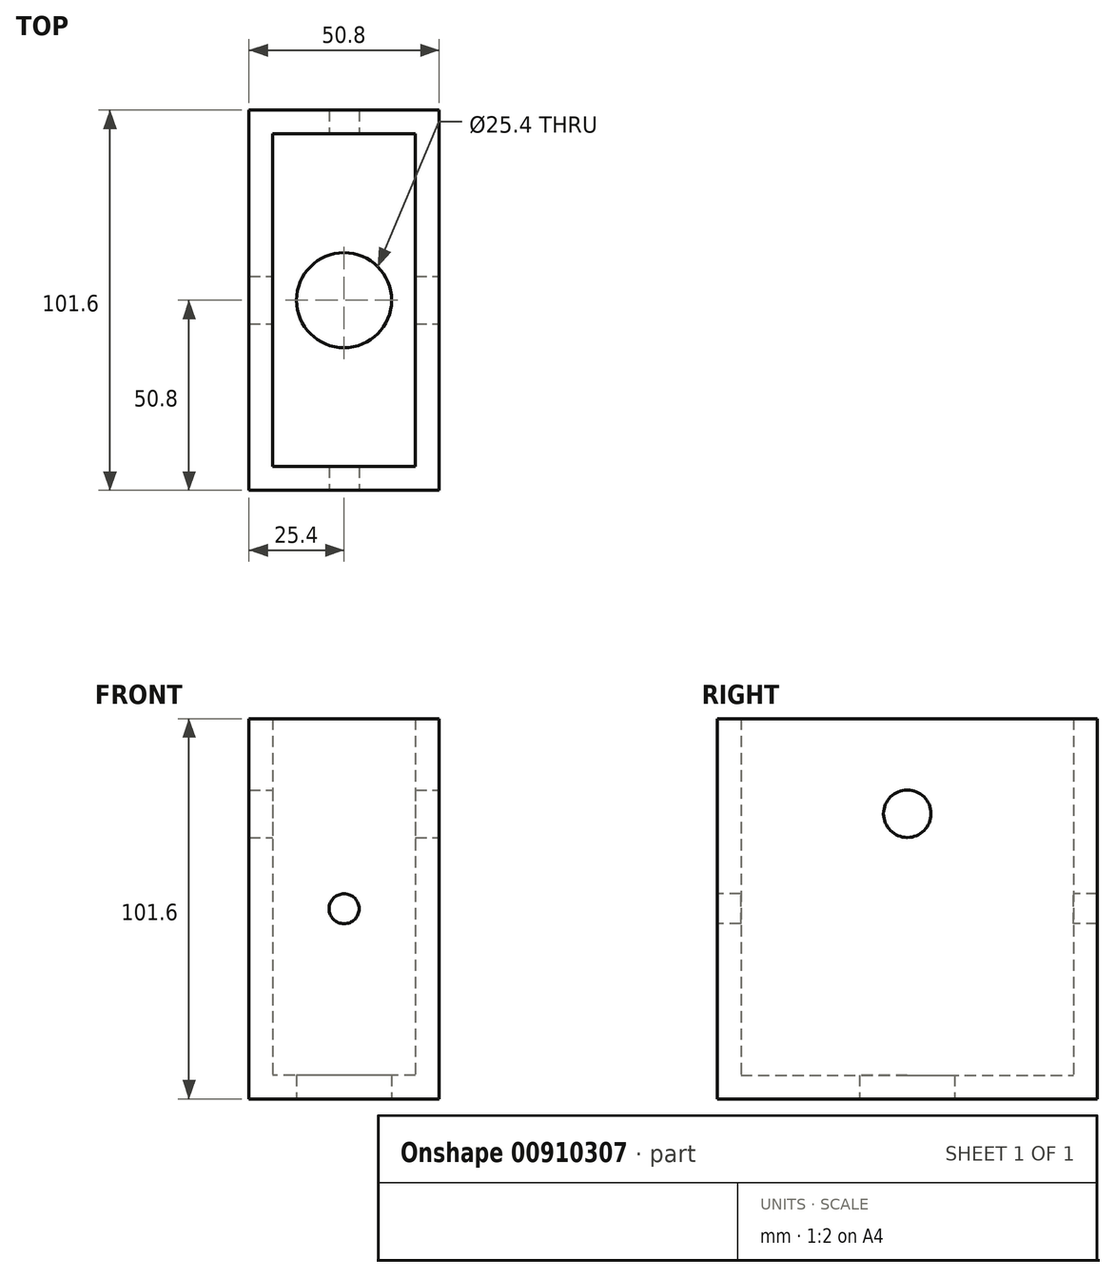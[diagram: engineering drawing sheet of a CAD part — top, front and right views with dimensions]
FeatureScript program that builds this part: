
annotation { "Feature Type Name" : "Feature", "Feature Type Description" : "" }
export const myFeature = defineFeature(function(context is Context, id is Id, definition is map)
    precondition{}
    {
        {
            var Q0;
            Q0=qCreatedBy(makeId("Top.planeOp"),FACE);
            var sketch = newSketch(context, id + "F0", { "sketchPlane" : qUnion([Q0])});
            skLineSegment(sketch, "E0.bottom", {"start": v(25.4, -50.8) * mm, "end": v(-25.4, -50.8) * mm});
            skLineSegment(sketch, "E0.top", {"start": v(25.4, 50.8) * mm, "end": v(-25.4, 50.8) * mm});
            skLineSegment(sketch, "E0.left", {"start": v(25.4, -50.8) * mm, "end": v(25.4, 50.8) * mm});
            skLineSegment(sketch, "E0.right", {"start": v(-25.4, -50.8) * mm, "end": v(-25.4, 50.8) * mm});
            skPoint(sketch, "E0.middle", {"position": v(0, 0) * mm});
            skSolve(sketch);
        }
        {
            var Q0;
            Q0=makeQuery(id+"F0.imprint","IMPRINT",FACE,{"disambiguationData":[TD([[makeQuery(id+"F0.imprint","IMPRINT",EDGE,{"derivedFrom":sQuery(id+"F0.wireOp",EDGE,"E0.bottom")}),-1.0]])]});
            extrude(context, id + "F1", {"entities" : qUnion([Q0]), "depth" : 101.6 * mm, "offsetDistance" : 25.4 * mm});
        }
        {
            var Q0;
            Q0=makeQuery(id+"F1.opExtrude","CAP_FACE",FACE,{"disambiguationData":[OSD([sQuery(id+"F0.wireOp",EDGE,"E0.bottom"),sQuery(id+"F0.wireOp",EDGE,"E0.top"),sQuery(id+"F0.wireOp",EDGE,"E0.left"),sQuery(id+"F0.wireOp",EDGE,"E0.right")])],"isStart":false});
            shell(context, id + "F2", {"entities" : qUnion([Q0]), "thickness" : 6.35 * mm});
        }
        {
            var Q0;
            Q0=makeQuery(id+"F1.opExtrude","SWEPT_FACE",FACE,{"disambiguationData":[OSD([sQuery(id+"F0.wireOp",EDGE,"E0.left")])]});
            var sketch = newSketch(context, id + "F3", { "sketchPlane" : qUnion([Q0])});
            skPoint(sketch, "E1", {"position": v(0, 76.2) * mm});
            skSolve(sketch);
        }
        {
            var Q0;
            Q0=sQuery(id+"F3.wireOp",VERTEX,"E1");
            var Q1;
            Q1=makeQuery(id+"F1.opExtrude","SWEPT_BODY",BODY,{"disambiguationData":[OSD([sQuery(id+"F0.wireOp",EDGE,"E0.bottom"),sQuery(id+"F0.wireOp",EDGE,"E0.top"),sQuery(id+"F0.wireOp",EDGE,"E0.left"),sQuery(id+"F0.wireOp",EDGE,"E0.right")])]});
            hole(context, id + "F4", {"style" : HoleStyle.SIMPLE, "endStyle" : HoleEndStyle.THROUGH, "holeDiameter" : 12.7 * mm, "majorDiameter" : 6.35 * mm, "isTappedThrough" : true, "tappedDepth" : 12.7 * mm, "tapClearance" : 3, "locations" : qUnion([Q0]), "scope" : qUnion([Q1])});
        }
        {
            var Q0;
            Q0=makeQuery(id+"F1.opExtrude","CAP_FACE",FACE,{"disambiguationData":[OSD([sQuery(id+"F0.wireOp",EDGE,"E0.bottom"),sQuery(id+"F0.wireOp",EDGE,"E0.top"),sQuery(id+"F0.wireOp",EDGE,"E0.left"),sQuery(id+"F0.wireOp",EDGE,"E0.right")])],"isStart":true});
            var sketch = newSketch(context, id + "F5", { "sketchPlane" : qUnion([Q0])});
            skPoint(sketch, "E2", {"position": v(0, 0) * mm});
            skSolve(sketch);
        }
        {
            var Q0;
            Q0=sQuery(id+"F5.wireOp",VERTEX,"E2");
            var Q1;
            Q1=makeQuery(id+"F1.opExtrude","SWEPT_BODY",BODY,{"disambiguationData":[OSD([sQuery(id+"F0.wireOp",EDGE,"E0.bottom"),sQuery(id+"F0.wireOp",EDGE,"E0.top"),sQuery(id+"F0.wireOp",EDGE,"E0.left"),sQuery(id+"F0.wireOp",EDGE,"E0.right")])]});
            hole(context, id + "F6", {"style" : HoleStyle.SIMPLE, "endStyle" : HoleEndStyle.BLIND, "holeDiameter" : 25.4 * mm, "majorDiameter" : 6.35 * mm, "holeDepth" : 25.4 * mm, "isTappedThrough" : true, "tappedDepth" : 12.7 * mm, "tapClearance" : 3, "locations" : qUnion([Q0]), "scope" : qUnion([Q1])});
        }
        {
            var Q0;
            Q0=makeQuery(id+"F1.opExtrude","SWEPT_FACE",FACE,{"disambiguationData":[OSD([sQuery(id+"F0.wireOp",EDGE,"E0.bottom")])]});
            var sketch = newSketch(context, id + "F7", { "sketchPlane" : qUnion([Q0])});
            skPoint(sketch, "E3", {"position": v(0, 50.8) * mm});
            skSolve(sketch);
        }
        {
            var Q0;
            Q0=sQuery(id+"F7.wireOp",VERTEX,"E3");
            var Q1;
            Q1=makeQuery(id+"F1.opExtrude","SWEPT_BODY",BODY,{"disambiguationData":[OSD([sQuery(id+"F0.wireOp",EDGE,"E0.bottom"),sQuery(id+"F0.wireOp",EDGE,"E0.top"),sQuery(id+"F0.wireOp",EDGE,"E0.left"),sQuery(id+"F0.wireOp",EDGE,"E0.right")])]});
            hole(context, id + "F8", {"style" : HoleStyle.SIMPLE, "endStyle" : HoleEndStyle.THROUGH, "holeDiameter" : 8 * mm, "majorDiameter" : 6.35 * mm, "isTappedThrough" : true, "tappedDepth" : 12.7 * mm, "tapClearance" : 3, "locations" : qUnion([Q0]), "scope" : qUnion([Q1])});
        }
    });
